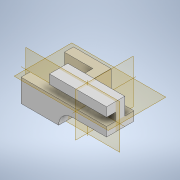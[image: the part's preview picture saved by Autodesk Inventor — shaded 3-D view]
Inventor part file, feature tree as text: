
AUTODESK INVENTOR PART (.ipt)
format: ipt  version: 2022.4 (Build 264492010, 492A)  size: 164,864 bytes
history: native  units: mm
features: extrude x4, sketch x4
ambient origin geometry x8: Origin, YZ Plane, XZ Plane, XY Plane, X Axis, Y Axis, Z Axis, Center Point
bodies: Solid1 (feature_tree)
feature tree (8):
  extrude  "Extrusion1"  Depth=3.0mm
  extrude  "Extrusion2"  Depth=1.6mm
  sketch  "Sketch4"  dims[d3=3.2mm d4=1.6mm]
  sketch  "Sketch5"  dims[d6=4.0mm d7=1.6mm]
  extrude  "Extrusion3"  Depth=1.6mm
  extrude  "Extrusion4"  Depth=10.0mm TaperAngle=0.0deg
  sketch  "Sketch3"  dims[d1=6.0mm d2=3.0mm]
  sketch  "Sketch6"  dims[d8=1.4mm d10=10.0mm d11=0.0mm d12=1.6mm d14=1.6mm d15=1.6mm d17=2.4mm d18=0.0mm d19=0.0mm d20=1.6mm d21=1.6mm d22=5.0mm d23=0.0mm d24=1.6mm d25=1.6mm d26=1.6mm d27=0.0mm d28=0.0mm]
